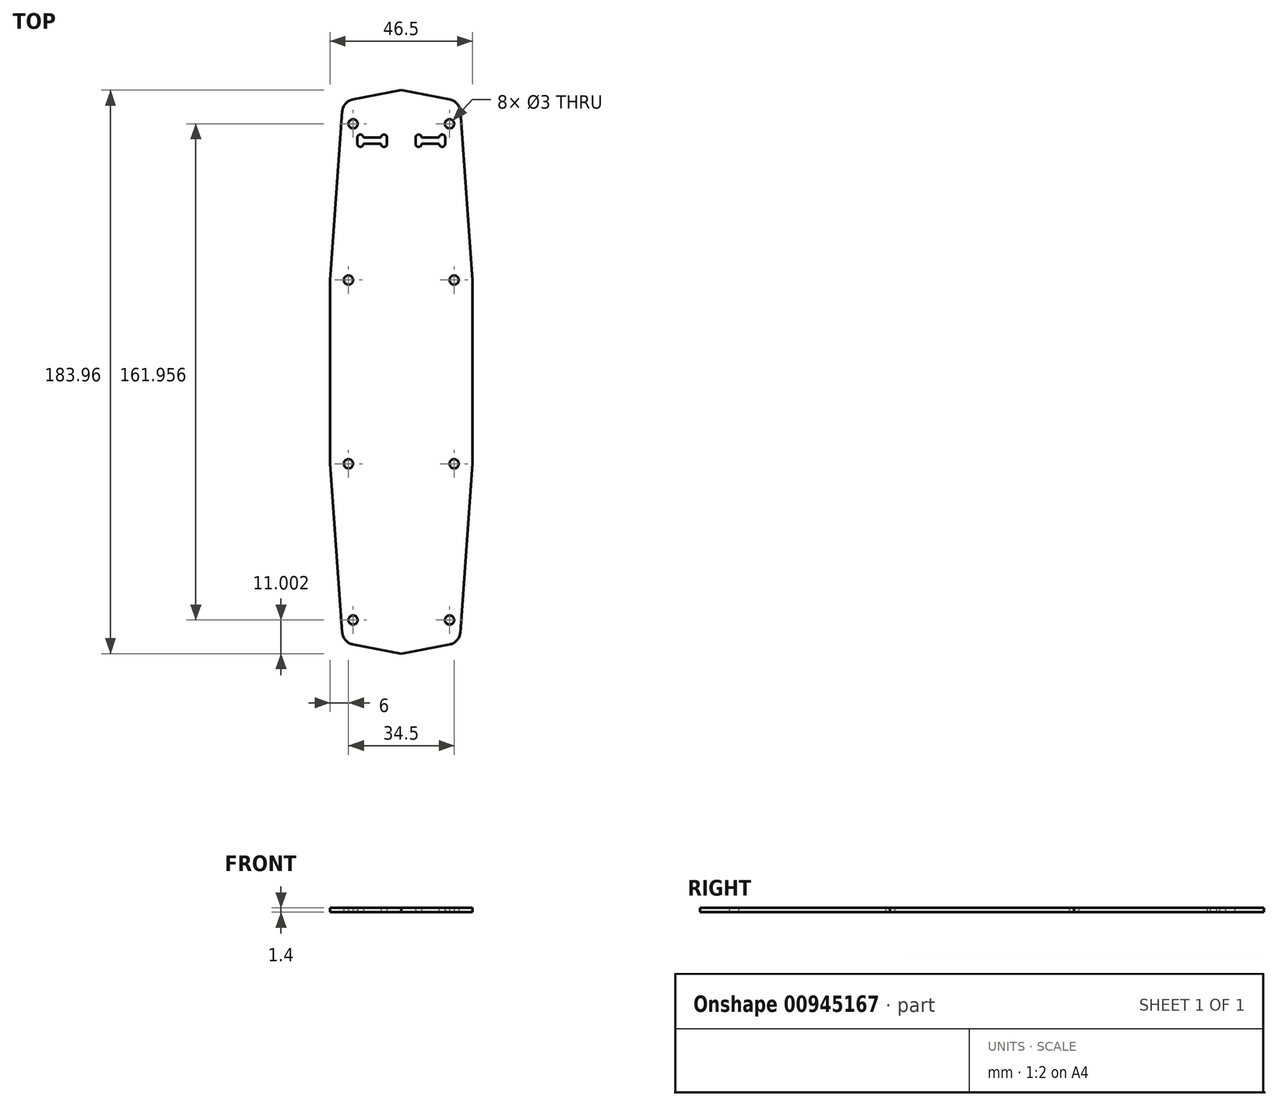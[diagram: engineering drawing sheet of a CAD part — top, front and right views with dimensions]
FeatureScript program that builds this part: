
annotation { "Feature Type Name" : "Feature", "Feature Type Description" : "" }
export const myFeature = defineFeature(function(context is Context, id is Id, definition is map)
    precondition{}
    {
        {
            var Q0;
            Q0=qCreatedBy(makeId("Top.planeOp"),FACE);
            var sketch = newSketch(context, id + "F0", { "sketchPlane" : qUnion([Q0])});
            skCircle(sketch, "E0", {"center": v(-15.75, 80.98) * mm, "radius": 1.5 * mm});
            skCircle(sketch, "E1", {"center": v(-17.25, 30) * mm, "radius": 1.5 * mm});
            skLineSegment(sketch, "E2", {"start": v(-19.55, 80.98) * mm, "end": v(-23.25, 30) * mm});
            skLineSegment(sketch, "E3", {"start": v(-23.25, 30) * mm, "end": v(-17.25, 30) * mm, "construction": true});
            skLineSegment(sketch, "E4", {"start": v(-15.75, 80.98) * mm, "end": v(-19.55, 80.98) * mm, "construction": true});
            skLineSegment(sketch, "E5", {"start": v(-23.25, 30) * mm, "end": v(-23.25, 0) * mm});
            skLineSegment(sketch, "E6", {"start": v(0, 91.98) * mm, "end": v(-15.75, 88.98) * mm});
            skLineSegment(sketch, "E7", {"start": v(-15.75, 88.98) * mm, "end": v(-15.75, 80.98) * mm, "construction": true});
            skArc(sketch, "E8", {"start": v(-15.75, 88.98) * mm, "mid": v(-18.17, 87.6) * mm, "end": v(-19.26, 85.04) * mm});
            skLineSegment(sketch, "E9", {"start": v(-19.26, 85.04) * mm, "end": v(-19.55, 80.98) * mm});
            skLineSegment(sketch, "E10.MirrorCS", {"start": v(0, 91.98) * mm, "end": v(15.75, 88.98) * mm});
            skArc(sketch, "E11.MirrorCS", {"start": v(15.75, 88.98) * mm, "mid": v(18.17, 87.6) * mm, "end": v(19.26, 85.04) * mm});
            skLineSegment(sketch, "E12.MirrorCS", {"start": v(19.55, 80.98) * mm, "end": v(23.25, 30) * mm});
            skLineSegment(sketch, "E13.MirrorCS", {"start": v(19.26, 85.04) * mm, "end": v(19.55, 80.98) * mm});
            skCircle(sketch, "E14.MirrorC", {"center": v(15.75, 80.98) * mm, "radius": 1.5 * mm});
            skLineSegment(sketch, "E15.MirrorCS", {"start": v(23.25, 30) * mm, "end": v(23.25, 0) * mm});
            skCircle(sketch, "E16.MirrorC", {"center": v(17.25, 30) * mm, "radius": 1.5 * mm});
            skLineSegment(sketch, "E17.MirrorCS", {"start": v(23.25, -30) * mm, "end": v(23.25, 0) * mm});
            skLineSegment(sketch, "E18.MirrorCS", {"start": v(19.55, -80.98) * mm, "end": v(23.25, -30) * mm});
            skArc(sketch, "E19.MirrorCS", {"start": v(15.75, -88.98) * mm, "mid": v(18.17, -87.6) * mm, "end": v(19.26, -85.04) * mm});
            skLineSegment(sketch, "E20.MirrorCS", {"start": v(19.26, -85.04) * mm, "end": v(19.55, -80.98) * mm});
            skLineSegment(sketch, "E21.MirrorCS", {"start": v(0, -91.98) * mm, "end": v(15.75, -88.98) * mm});
            skCircle(sketch, "E22.MirrorC", {"center": v(15.75, -80.98) * mm, "radius": 1.5 * mm});
            skArc(sketch, "E23.MirrorCS", {"start": v(-15.75, -88.98) * mm, "mid": v(-18.17, -87.6) * mm, "end": v(-19.26, -85.04) * mm});
            skLineSegment(sketch, "E24.MirrorCS", {"start": v(0, -91.98) * mm, "end": v(-15.75, -88.98) * mm});
            skCircle(sketch, "E25.MirrorC", {"center": v(-15.75, -80.98) * mm, "radius": 1.5 * mm});
            skLineSegment(sketch, "E26.MirrorCS", {"start": v(-19.26, -85.04) * mm, "end": v(-19.55, -80.98) * mm});
            skLineSegment(sketch, "E27.MirrorCS", {"start": v(-19.55, -80.98) * mm, "end": v(-23.25, -30) * mm});
            skLineSegment(sketch, "E28.MirrorCS", {"start": v(-23.25, -30) * mm, "end": v(-23.25, 0) * mm});
            skCircle(sketch, "E29.MirrorC", {"center": v(-17.25, -30) * mm, "radius": 1.5 * mm});
            skCircle(sketch, "E30.MirrorC", {"center": v(17.25, -30) * mm, "radius": 1.5 * mm});
            skLineSegment(sketch, "E31", {"start": v(-14.35, 75.48) * mm, "end": v(-14.35, 74.48) * mm});
            skLineSegment(sketch, "E32", {"start": v(-13.35, 73.48) * mm, "end": v(-13.35, 73.48) * mm});
            skLineSegment(sketch, "E33", {"start": v(-12.35, 74.48) * mm, "end": v(-12.35, 74.48) * mm});
            skLineSegment(sketch, "E34", {"start": v(-12.35, 74.48) * mm, "end": v(-9.5, 74.48) * mm});
            skLineSegment(sketch, "E35", {"start": v(-9.5, 74.48) * mm, "end": v(-9.5, 75.48) * mm, "construction": true});
            skLineSegment(sketch, "E36", {"start": v(-9.5, 75.48) * mm, "end": v(-14.35, 75.48) * mm, "construction": true});
            skLineSegment(sketch, "E37.MirrorCS", {"start": v(-12.35, 76.48) * mm, "end": v(-9.5, 76.48) * mm});
            skLineSegment(sketch, "E38.MirrorCS", {"start": v(-6.65, 74.48) * mm, "end": v(-9.5, 74.48) * mm});
            skLineSegment(sketch, "E39.MirrorCS", {"start": v(-6.65, 76.48) * mm, "end": v(-9.5, 76.48) * mm});
            skLineSegment(sketch, "E40", {"start": v(-6.65, 76.48) * mm, "end": v(-6.65, 74.48) * mm, "construction": true});
            skPoint(sketch, "E41.visualSharp", {"position": v(-14.35, 73.48) * mm});
            skArc(sketch, "E41.filletArc", {"start": v(-14.35, 74.48) * mm, "mid": v(-14.06, 73.77) * mm, "end": v(-13.35, 73.48) * mm});
            skPoint(sketch, "E42.visualSharp", {"position": v(-12.35, 73.48) * mm});
            skArc(sketch, "E42.filletArc", {"start": v(-13.35, 73.48) * mm, "mid": v(-12.64, 73.77) * mm, "end": v(-12.35, 74.48) * mm});
            skLineSegment(sketch, "E43.MirrorCS", {"start": v(-14.35, 75.48) * mm, "end": v(-14.35, 76.48) * mm});
            skArc(sketch, "E44.MirrorCS", {"start": v(-14.35, 76.48) * mm, "mid": v(-14.06, 77.19) * mm, "end": v(-13.35, 77.48) * mm});
            skArc(sketch, "E45.MirrorCS", {"start": v(-13.35, 77.48) * mm, "mid": v(-12.64, 77.19) * mm, "end": v(-12.35, 76.48) * mm});
            skPoint(sketch, "E46.MirrorP", {"position": v(-14.35, 77.48) * mm});
            skLineSegment(sketch, "E47.MirrorCS", {"start": v(-13.35, 77.48) * mm, "end": v(-13.35, 77.48) * mm});
            skPoint(sketch, "E48.MirrorP", {"position": v(-12.35, 77.48) * mm});
            skLineSegment(sketch, "E49.MirrorCS", {"start": v(-12.35, 76.48) * mm, "end": v(-12.35, 76.48) * mm});
            skArc(sketch, "E50.MirrorCS", {"start": v(-5.65, 73.48) * mm, "mid": v(-6.36, 73.77) * mm, "end": v(-6.65, 74.48) * mm});
            skArc(sketch, "E51.MirrorCS", {"start": v(-4.65, 74.48) * mm, "mid": v(-4.94, 73.77) * mm, "end": v(-5.65, 73.48) * mm});
            skPoint(sketch, "E52.MirrorP", {"position": v(-6.65, 73.48) * mm});
            skPoint(sketch, "E53.MirrorP", {"position": v(-4.65, 73.48) * mm});
            skLineSegment(sketch, "E54.MirrorCS", {"start": v(-5.65, 73.48) * mm, "end": v(-5.65, 73.48) * mm});
            skArc(sketch, "E55.MirrorCS", {"start": v(-4.65, 76.48) * mm, "mid": v(-4.94, 77.19) * mm, "end": v(-5.65, 77.48) * mm});
            skArc(sketch, "E56.MirrorCS", {"start": v(-5.65, 77.48) * mm, "mid": v(-6.36, 77.19) * mm, "end": v(-6.65, 76.48) * mm});
            skPoint(sketch, "E57.MirrorP", {"position": v(-6.65, 77.48) * mm});
            skPoint(sketch, "E58.MirrorP", {"position": v(-4.65, 77.48) * mm});
            skLineSegment(sketch, "E59.MirrorCS", {"start": v(-5.65, 77.48) * mm, "end": v(-5.65, 77.48) * mm});
            skLineSegment(sketch, "E60.MirrorCS", {"start": v(-6.65, 76.48) * mm, "end": v(-6.65, 76.48) * mm});
            skLineSegment(sketch, "E61.MirrorCS", {"start": v(-4.65, 75.48) * mm, "end": v(-4.65, 76.48) * mm});
            skLineSegment(sketch, "E62.MirrorCS", {"start": v(-4.65, 75.48) * mm, "end": v(-4.65, 74.48) * mm});
            skLineSegment(sketch, "E63.MirrorCS", {"start": v(-6.65, 74.48) * mm, "end": v(-6.65, 74.48) * mm});
            skLineSegment(sketch, "E64", {"start": v(-6.65, 76.48) * mm, "end": v(-4.65, 76.48) * mm, "construction": true});
            skLineSegment(sketch, "E65.MirrorCS", {"start": v(9.5, 74.48) * mm, "end": v(9.5, 75.48) * mm, "construction": true});
            skPoint(sketch, "E66.MirrorP", {"position": v(6.65, 77.48) * mm});
            skLineSegment(sketch, "E67.MirrorCS", {"start": v(6.65, 76.48) * mm, "end": v(6.65, 76.48) * mm});
            skArc(sketch, "E68.MirrorCS", {"start": v(14.35, 76.48) * mm, "mid": v(14.06, 77.19) * mm, "end": v(13.35, 77.48) * mm});
            skLineSegment(sketch, "E69.MirrorCS", {"start": v(6.65, 76.48) * mm, "end": v(6.65, 74.48) * mm, "construction": true});
            skLineSegment(sketch, "E70.MirrorCS", {"start": v(12.35, 74.48) * mm, "end": v(9.5, 74.48) * mm});
            skArc(sketch, "E71.MirrorCS", {"start": v(13.35, 77.48) * mm, "mid": v(12.64, 77.19) * mm, "end": v(12.35, 76.48) * mm});
            skLineSegment(sketch, "E72.MirrorCS", {"start": v(14.35, 75.48) * mm, "end": v(14.35, 76.48) * mm});
            skLineSegment(sketch, "E73.MirrorCS", {"start": v(4.65, 75.48) * mm, "end": v(4.65, 74.48) * mm});
            skPoint(sketch, "E74.MirrorP", {"position": v(14.35, 73.48) * mm});
            skArc(sketch, "E75.MirrorCS", {"start": v(13.35, 73.48) * mm, "mid": v(12.64, 73.77) * mm, "end": v(12.35, 74.48) * mm});
            skArc(sketch, "E76.MirrorCS", {"start": v(5.65, 73.48) * mm, "mid": v(6.36, 73.77) * mm, "end": v(6.65, 74.48) * mm});
            skPoint(sketch, "E77.MirrorP", {"position": v(14.35, 77.48) * mm});
            skLineSegment(sketch, "E78.MirrorCS", {"start": v(6.65, 74.48) * mm, "end": v(6.65, 74.48) * mm});
            skLineSegment(sketch, "E79.MirrorCS", {"start": v(6.65, 74.48) * mm, "end": v(9.5, 74.48) * mm});
            skLineSegment(sketch, "E80.MirrorCS", {"start": v(13.35, 73.48) * mm, "end": v(13.35, 73.48) * mm});
            skPoint(sketch, "E81.MirrorP", {"position": v(4.65, 77.48) * mm});
            skLineSegment(sketch, "E82.MirrorCS", {"start": v(5.65, 73.48) * mm, "end": v(5.65, 73.48) * mm});
            skLineSegment(sketch, "E83.MirrorCS", {"start": v(14.35, 75.48) * mm, "end": v(14.35, 74.48) * mm});
            skLineSegment(sketch, "E84.MirrorCS", {"start": v(13.35, 77.48) * mm, "end": v(13.35, 77.48) * mm});
            skPoint(sketch, "E85.MirrorP", {"position": v(12.35, 73.48) * mm});
            skArc(sketch, "E86.MirrorCS", {"start": v(14.35, 74.48) * mm, "mid": v(14.06, 73.77) * mm, "end": v(13.35, 73.48) * mm});
            skLineSegment(sketch, "E87.MirrorCS", {"start": v(5.65, 77.48) * mm, "end": v(5.65, 77.48) * mm});
            skPoint(sketch, "E88.MirrorP", {"position": v(6.65, 73.48) * mm});
            skLineSegment(sketch, "E89.MirrorCS", {"start": v(6.65, 76.48) * mm, "end": v(9.5, 76.48) * mm});
            skArc(sketch, "E90.MirrorCS", {"start": v(4.65, 74.48) * mm, "mid": v(4.94, 73.77) * mm, "end": v(5.65, 73.48) * mm});
            skLineSegment(sketch, "E91.MirrorCS", {"start": v(4.65, 75.48) * mm, "end": v(4.65, 76.48) * mm});
            skArc(sketch, "E92.MirrorCS", {"start": v(4.65, 76.48) * mm, "mid": v(4.94, 77.19) * mm, "end": v(5.65, 77.48) * mm});
            skLineSegment(sketch, "E93.MirrorCS", {"start": v(12.35, 76.48) * mm, "end": v(9.5, 76.48) * mm});
            skArc(sketch, "E94.MirrorCS", {"start": v(5.65, 77.48) * mm, "mid": v(6.36, 77.19) * mm, "end": v(6.65, 76.48) * mm});
            skLineSegment(sketch, "E95.MirrorCS", {"start": v(9.5, 75.48) * mm, "end": v(14.35, 75.48) * mm, "construction": true});
            skPoint(sketch, "E96.MirrorP", {"position": v(12.35, 77.48) * mm});
            skLineSegment(sketch, "E97.MirrorCS", {"start": v(12.35, 76.48) * mm, "end": v(12.35, 76.48) * mm});
            skLineSegment(sketch, "E98.MirrorCS", {"start": v(12.35, 74.48) * mm, "end": v(12.35, 74.48) * mm});
            skLineSegment(sketch, "E99.MirrorCS", {"start": v(6.65, 76.48) * mm, "end": v(4.65, 76.48) * mm, "construction": true});
            skPoint(sketch, "E100.MirrorP", {"position": v(4.65, 73.48) * mm});
            skSolve(sketch);
        }
        {
            var Q0;
            Q0=makeQuery(id+"F0.imprint","IMPRINT",FACE,{"disambiguationData":[TD([[makeQuery(id+"F0.imprint","IMPRINT",EDGE,{"derivedFrom":sQuery(id+"F0.wireOp",EDGE,"E0")}),-1.0]])]});
            extrude(context, id + "F1", {"entities" : qUnion([Q0]), "depth" : 1.4 * mm, "offsetDistance" : 25 * mm});
        }
    });
